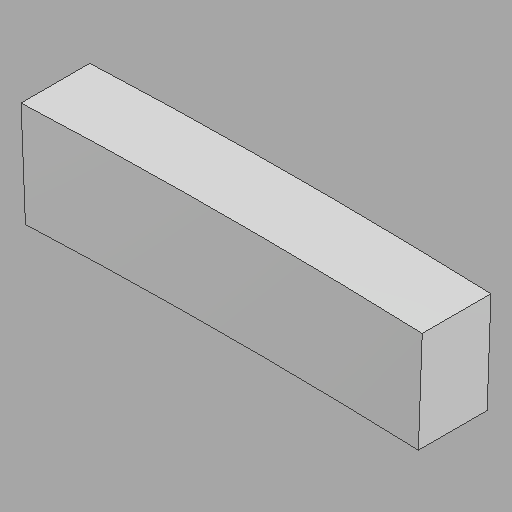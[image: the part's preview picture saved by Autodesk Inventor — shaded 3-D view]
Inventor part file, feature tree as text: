
AUTODESK INVENTOR PART (.ipt)
format: ipt  version: 2022.1 (Build 261234020, 234B)  size: 89,088 bytes
history: imported  units: in
note: dims shown in document units (in); Inventor stores cm internally (conversion verified against a paired STEP export)
features: imported_body x1
ambient origin geometry x8: Origin, YZ Plane, XZ Plane, XY Plane, X Axis, Y Axis, Z Axis, Center Point
bodies: Solid1 (imported_parasolid), Body1 (imported_parasolid)
feature tree (1):
  imported_body  NMx_Import_Brep_tag  [imported B-rep: ~7 faces, bbox_mm=[889.31347, 231.163309, 152.4]]
